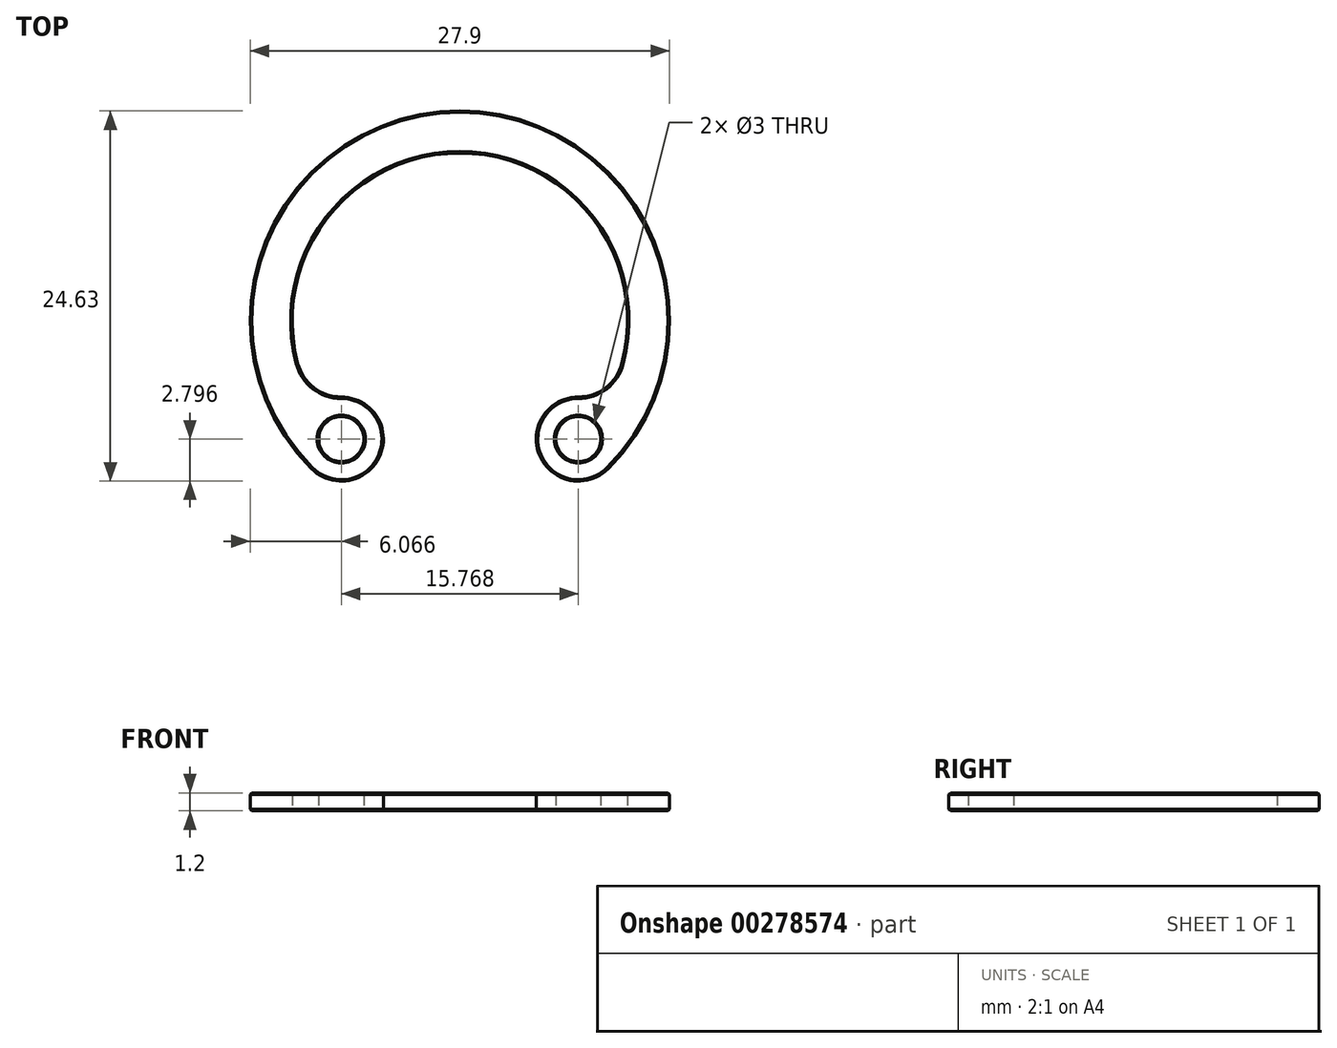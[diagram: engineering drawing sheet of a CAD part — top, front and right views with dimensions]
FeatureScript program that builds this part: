
annotation { "Feature Type Name" : "Feature", "Feature Type Description" : "" }
export const myFeature = defineFeature(function(context is Context, id is Id, definition is map)
    precondition{}
    {
        {
            var Q0;
            Q0=qCreatedBy(makeId("Top.planeOp"),FACE);
            var sketch = newSketch(context, id + "F0", { "sketchPlane" : qUnion([Q0])});
            skCircle(sketch, "E0", {"center": v(0, 0) * mm, "radius": 13.95 * mm});
            skCircle(sketch, "E1", {"center": v(0, 0) * mm, "radius": 11.15 * mm});
            skLineSegment(sketch, "E2", {"start": v(0, 0) * mm, "end": v(0, -17.01) * mm, "construction": true});
            skLineSegment(sketch, "E3", {"start": v(0, 0) * mm, "end": v(17.01, -17.01) * mm, "construction": true});
            skLineSegment(sketch, "E4", {"start": v(0, 0) * mm, "end": v(-17.01, -17.01) * mm, "construction": true});
            skCircle(sketch, "E5", {"center": v(-7.88, -7.88) * mm, "radius": 2.8 * mm});
            skCircle(sketch, "E6", {"center": v(7.88, -7.88) * mm, "radius": 2.8 * mm});
            skCircle(sketch, "E7", {"center": v(7.88, -7.88) * mm, "radius": 1.5 * mm});
            skCircle(sketch, "E8", {"center": v(-7.88, -7.88) * mm, "radius": 1.5 * mm});
            skSolve(sketch);
        }
        {
            var Q0;
            {var subQ0=sQuery(id+"F0.wireOp",EDGE,"E5");var subQ1=sQuery(id+"F0.wireOp",EDGE,"E0");var subQ2=makeQuery(id+"F0.imprint","INTERSECT",VERTEX,{"derivedFrom":[subQ1,subQ0]});Q0=makeQuery(id+"F0.imprint","IMPRINT",FACE,{"disambiguationData":[TD([[makeQuery(id+"F0.imprint","IMPRINT",EDGE,{"disambiguationData":[TD([[subQ2,1.0]])],"derivedFrom":subQ1}),1.0]])]});}
            var Q1;
            {var subQ0=sQuery(id+"F0.wireOp",EDGE,"E8");var subQ1=sQuery(id+"F0.wireOp",EDGE,"E1");var subQ2=makeQuery(id+"F0.imprint","INTERSECT",VERTEX,{"disambiguationData":[OD(0.0)],"derivedFrom":[subQ1,subQ0]});Q1=makeQuery(id+"F0.imprint","IMPRINT",FACE,{"disambiguationData":[TD([[makeQuery(id+"F0.imprint","IMPRINT",EDGE,{"disambiguationData":[TD([[subQ2,1.0]])],"derivedFrom":subQ1}),1.0]])]});}
            var Q2;
            {var subQ2=sQuery(id+"F0.wireOp",EDGE,"E1");var subQ5=sQuery(id+"F0.wireOp",EDGE,"E8");var subQ7=makeQuery(id+"F0.imprint","INTERSECT",VERTEX,{"disambiguationData":[OD(0.0)],"derivedFrom":[subQ2,subQ5]});Q2=makeQuery(id+"F0.imprint","IMPRINT",FACE,{"disambiguationData":[TD([[makeQuery(id+"F0.imprint","IMPRINT",EDGE,{"disambiguationData":[TD([[subQ7,1.0]])],"derivedFrom":subQ2}),-1.0]])]});}
            var Q3;
            {var subQ0=sQuery(id+"F0.wireOp",EDGE,"E6");var subQ1=sQuery(id+"F0.wireOp",EDGE,"E1");var subQ2=makeQuery(id+"F0.imprint","INTERSECT",VERTEX,{"disambiguationData":[OD(0.0)],"derivedFrom":[subQ1,subQ0]});Q3=makeQuery(id+"F0.imprint","IMPRINT",FACE,{"disambiguationData":[TD([[makeQuery(id+"F0.imprint","IMPRINT",EDGE,{"disambiguationData":[TD([[subQ2,-1.0]])],"derivedFrom":subQ1}),1.0]])]});}
            var Q4;
            {var subQ0=sQuery(id+"F0.wireOp",EDGE,"E6");var subQ2=sQuery(id+"F0.wireOp",EDGE,"E1");var subQ4=makeQuery(id+"F0.imprint","INTERSECT",VERTEX,{"disambiguationData":[OD(0.0)],"derivedFrom":[subQ2,subQ0]});Q4=makeQuery(id+"F0.imprint","IMPRINT",FACE,{"disambiguationData":[TD([[makeQuery(id+"F0.imprint","IMPRINT",EDGE,{"disambiguationData":[TD([[subQ4,-1.0]])],"derivedFrom":subQ2}),-1.0]])]});}
            extrude(context, id + "F1", {"entities" : qUnion([Q0, Q1, Q2, Q3, Q4]), "depth" : 1.2 * mm});
        }
        {
            var Q0;
            Q0=makeQuery(id+"F1.opExtrude","SWEPT_EDGE",EDGE,{"disambiguationData":[OSD([sQuery(id+"F0.wireOp",EDGE,"E1"),sQuery(id+"F0.wireOp",EDGE,"E5")])]});
            var Q1;
            Q1=makeQuery(id+"F1.opExtrude","SWEPT_EDGE",EDGE,{"disambiguationData":[OSD([sQuery(id+"F0.wireOp",EDGE,"E1"),sQuery(id+"F0.wireOp",EDGE,"E6")])]});
            fillet(context, id + "F2", {"entities" : qUnion([Q0, Q1]), "radius" : 3 * mm, "tangentPropagation" : true, "allowEdgeOverflow" : false});
        }
        {
            var Q0;
            Q0=makeQuery(id+"F1.opExtrude","CAP_FACE",FACE,{"disambiguationData":[OSD([sQuery(id+"F0.wireOp",EDGE,"E0"),sQuery(id+"F0.wireOp",EDGE,"E1"),sQuery(id+"F0.wireOp",EDGE,"E5"),sQuery(id+"F0.wireOp",EDGE,"E6"),sQuery(id+"F0.wireOp",EDGE,"E7"),sQuery(id+"F0.wireOp",EDGE,"E8")])],"isStart":false});
            var Q1;
            Q1=makeQuery(id+"F1.opExtrude","CAP_EDGE",EDGE,{"disambiguationData":[OSD([sQuery(id+"F0.wireOp",EDGE,"E1")])],"isStart":true});
            var Q2;
            Q2=makeQuery(id+"F1.opExtrude","CAP_EDGE",EDGE,{"disambiguationData":[OSD([sQuery(id+"F0.wireOp",EDGE,"E8")])],"isStart":true});
            var Q3;
            Q3=makeQuery(id+"F1.opExtrude","CAP_EDGE",EDGE,{"disambiguationData":[OSD([sQuery(id+"F0.wireOp",EDGE,"E7")])],"isStart":true});
            chamfer(context, id + "F3", {"entities" : qUnion([Q0, Q1, Q2, Q3]), "width" : 0.1 * mm, "tangentPropagation" : true});
        }
    });
